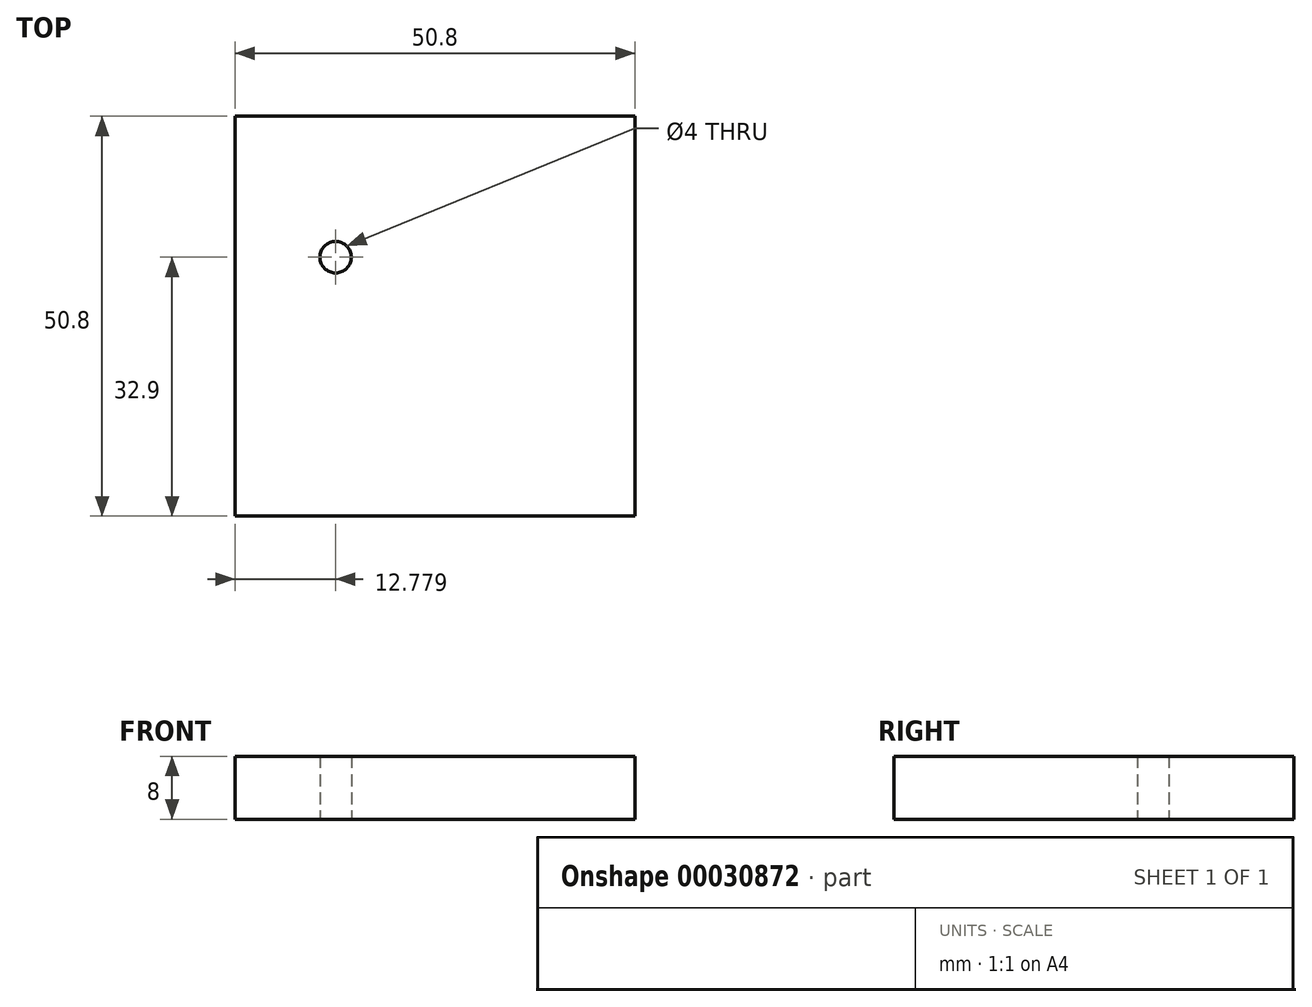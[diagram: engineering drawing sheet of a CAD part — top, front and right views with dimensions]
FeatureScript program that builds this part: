
annotation { "Feature Type Name" : "Feature", "Feature Type Description" : "" }
export const myFeature = defineFeature(function(context is Context, id is Id, definition is map)
    precondition{}
    {
        {
            var Q0;
            Q0=qCreatedBy(makeId("Top.planeOp"),FACE);
            var sketch = newSketch(context, id + "F0", { "sketchPlane" : qUnion([Q0])});
            skLineSegment(sketch, "E0.rect.bottom", {"start": v(25.4, -25.4) * mm, "end": v(-25.4, -25.4) * mm});
            skLineSegment(sketch, "E0.rect.top", {"start": v(25.4, 25.4) * mm, "end": v(-25.4, 25.4) * mm});
            skLineSegment(sketch, "E0.rect.left", {"start": v(25.4, -25.4) * mm, "end": v(25.4, 25.4) * mm});
            skLineSegment(sketch, "E0.rect.right", {"start": v(-25.4, -25.4) * mm, "end": v(-25.4, 25.4) * mm});
            skPoint(sketch, "E0.rect.middle", {"position": v(0, 0) * mm});
            skCircle(sketch, "E1", {"center": v(-15, -12.7) * mm, "radius": 4 * mm, "construction": true});
            skCircle(sketch, "E2", {"center": v(15, -12.7) * mm, "radius": 4 * mm, "construction": true});
            skSolve(sketch);
        }
        {
            var Q0;
            Q0 = qSketchRegion(id + "F0", true);
            extrude(context, id + "F1", {"entities" : qUnion([Q0]), "depth" : 8 * mm});
        }
        {
            var Q0;
            Q0=qCreatedBy(makeId("Top.planeOp"),FACE);
            var sketch = newSketch(context, id + "F2", { "sketchPlane" : qUnion([Q0])});
            skLineSegment(sketch, "E3", {"start": v(46.48, 7.5) * mm, "end": v(-46.93, 7.5) * mm, "construction": true});
            skCircle(sketch, "E4", {"center": v(-12.62, 7.5) * mm, "radius": 2 * mm});
            skCircle(sketch, "E5.MirrorC", {"center": v(12.62, 7.5) * mm, "radius": 2 * mm});
            skSolve(sketch);
        }
        {
            var Q0;
            Q0=makeQuery(id+"F2.imprint","IMPRINT",FACE,{"disambiguationData":[TD([[makeQuery(id+"F2.imprint","IMPRINT",EDGE,{"derivedFrom":sQuery(id+"F2.wireOp",EDGE,"E4")}),1.0]])]});
            var Q1;
            Q1=makeQuery(id+"F2.imprint","IMPRINT",FACE,{"disambiguationData":[TD([[makeQuery(id+"F2.imprint","IMPRINT",EDGE,{"derivedFrom":sQuery(id+"F2.wireOp",EDGE,"E5.MirrorC")}),-1.0]])]});
            extrude(context, id + "F3", {"entities" : qUnion([Q0, Q1]), "operationType" : NewBodyOperationType.REMOVE, "endBound" : BoundingType.UP_TO_NEXT, "depth" : 25.4 * mm});
        }
    });
